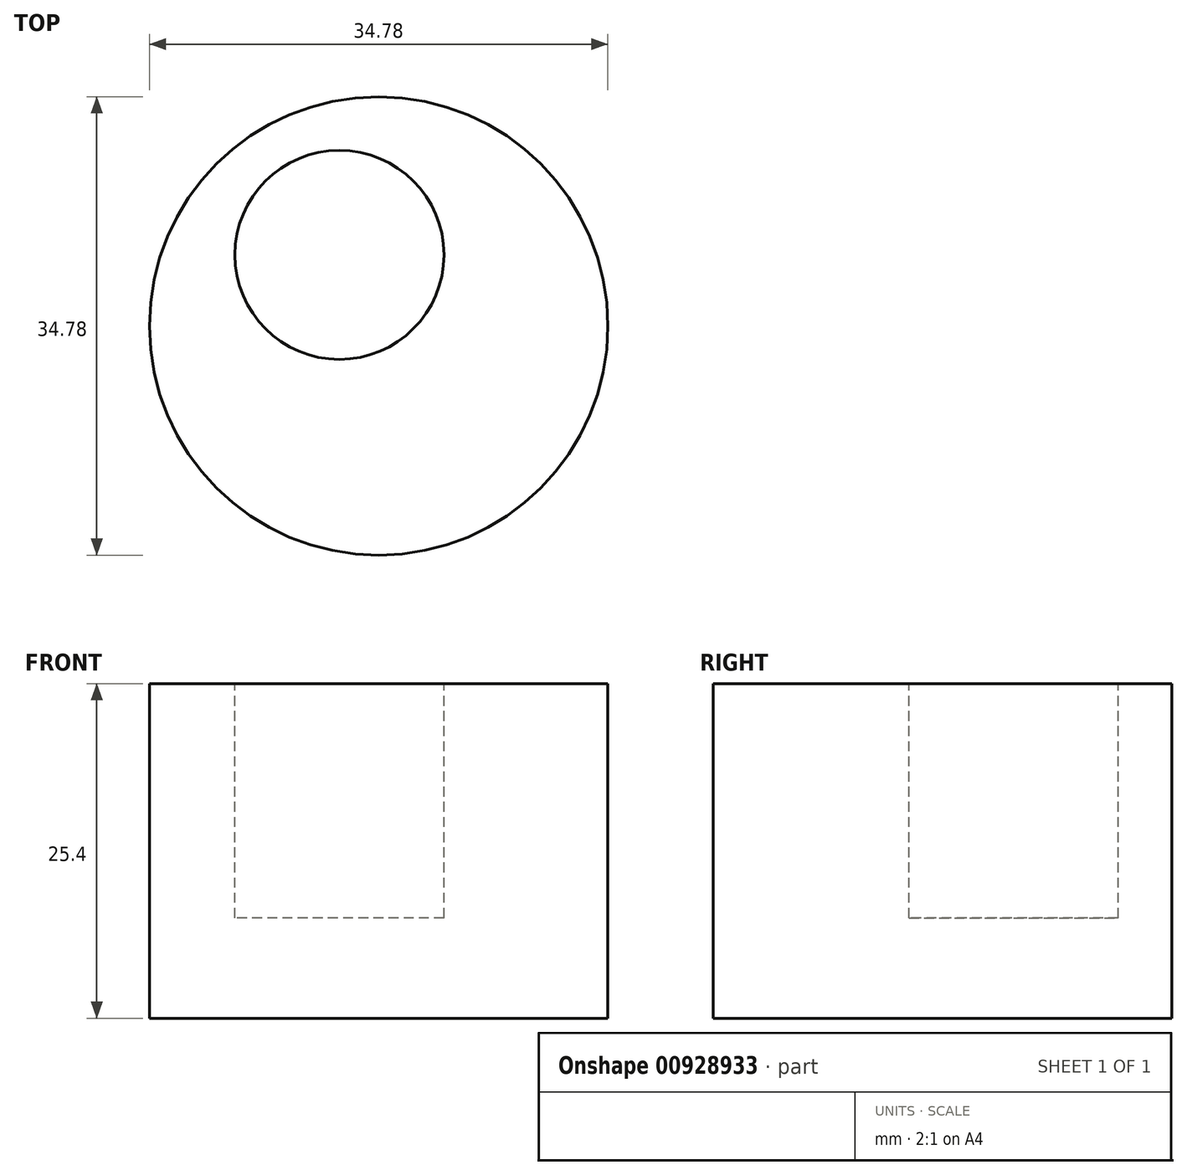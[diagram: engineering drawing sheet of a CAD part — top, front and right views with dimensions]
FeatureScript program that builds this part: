
annotation { "Feature Type Name" : "Feature", "Feature Type Description" : "" }
export const myFeature = defineFeature(function(context is Context, id is Id, definition is map)
    precondition{}
    {
        {
            var Q0;
            Q0=qCreatedBy(makeId("Top.planeOp"),FACE);
            var sketch = newSketch(context, id + "F0", { "sketchPlane" : qUnion([Q0])});
            skCircle(sketch, "E0", {"center": v(-36.75, 48.47) * mm, "radius": 17.4 * mm});
            skArc(sketch, "E1", {"start": v(-21.3, 56.47) * mm, "mid": v(37.1, 47.6) * mm, "end": v(59.96, -6.85) * mm});
            skSolve(sketch);
        }
        {
            var Q0;
            Q0=makeQuery(id+"F0.imprint","IMPRINT",FACE,{"disambiguationData":[TD([[makeQuery(id+"F0.imprint","IMPRINT",EDGE,{"derivedFrom":sQuery(id+"F0.wireOp",EDGE,"E0")}),1.0]])]});
            extrude(context, id + "F1", {"entities" : qUnion([Q0]), "depth" : 25.4 * mm, "offsetDistance" : 25.4 * mm});
        }
        {
            var Q0;
            Q0=makeQuery(id+"F1.opExtrude","CAP_FACE",FACE,{"disambiguationData":[OSD([sQuery(id+"F0.wireOp",EDGE,"E0")])],"isStart":false});
            var sketch = newSketch(context, id + "F2", { "sketchPlane" : qUnion([Q0])});
            skCircle(sketch, "E2", {"center": v(-39.73, 53.87) * mm, "radius": 7.93 * mm});
            skSolve(sketch);
        }
        {
            var Q0;
            Q0=makeQuery(id+"F2.imprint","IMPRINT",FACE,{"disambiguationData":[TD([[makeQuery(id+"F2.imprint","IMPRINT",EDGE,{"derivedFrom":sQuery(id+"F2.wireOp",EDGE,"E2")}),1.0]])]});
            extrude(context, id + "F3", {"entities" : qUnion([Q0]), "operationType" : NewBodyOperationType.REMOVE, "oppositeDirection" : true, "depth" : 17.78 * mm, "offsetDistance" : 25.4 * mm});
        }
    });
